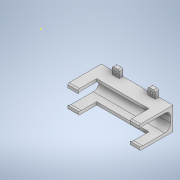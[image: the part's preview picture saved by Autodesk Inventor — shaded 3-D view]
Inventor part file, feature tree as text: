
AUTODESK INVENTOR PART (.ipt)
format: ipt  version: 2020 (Build 240168000, 168)  size: 216,064 bytes
history: native  units: in
note: dims shown in document units (in); Inventor stores cm internally (conversion verified against a paired STEP export)
features: sketch x5, extrude x4, plane x2, fillet x2
ambient origin geometry x8: Origin, YZ Plane, XZ Plane, XY Plane, X Axis, Y Axis, Z Axis, Center Point
bodies: Solid1 (feature_tree)
feature tree (13):
  sketch  "Sketch1"  dims[d1=1.8504in d2=0.0in d3=0.1969in d4=0.0in]
  extrude  "Extrusion1"  Depth=0.1969in TaperAngle=0.0deg
  extrude  "Extrusion2"  TaperAngle=0.0deg  [1 undecoded]
  plane  "Work Plane1"
  sketch  "Sketch3"  dims[d7=4.3307in d8=0.0in d9=1.5748in d10=0.0in]
  plane  "Work Plane2"
  extrude  "Extrusion3"  Depth=1.5748in TaperAngle=0.0deg
  extrude  "Extrusion4"  Depth=0.0787in
  fillet  "Fillet1"  [1 undecoded]
  fillet  "Fillet2"  [1 undecoded]
  sketch  "Sketch4"  dims[d11=0.0787in d12=0.0787in]
  sketch  "Sketch5"
  sketch  "Sketch2"  dims[d5=0.0in d6=0.0in]
note: 3 required parameter values undecoded (feature->parameter linkage not recoverable at this tier; creation-order binding heuristic only, values carry confidence <= 0.55)
